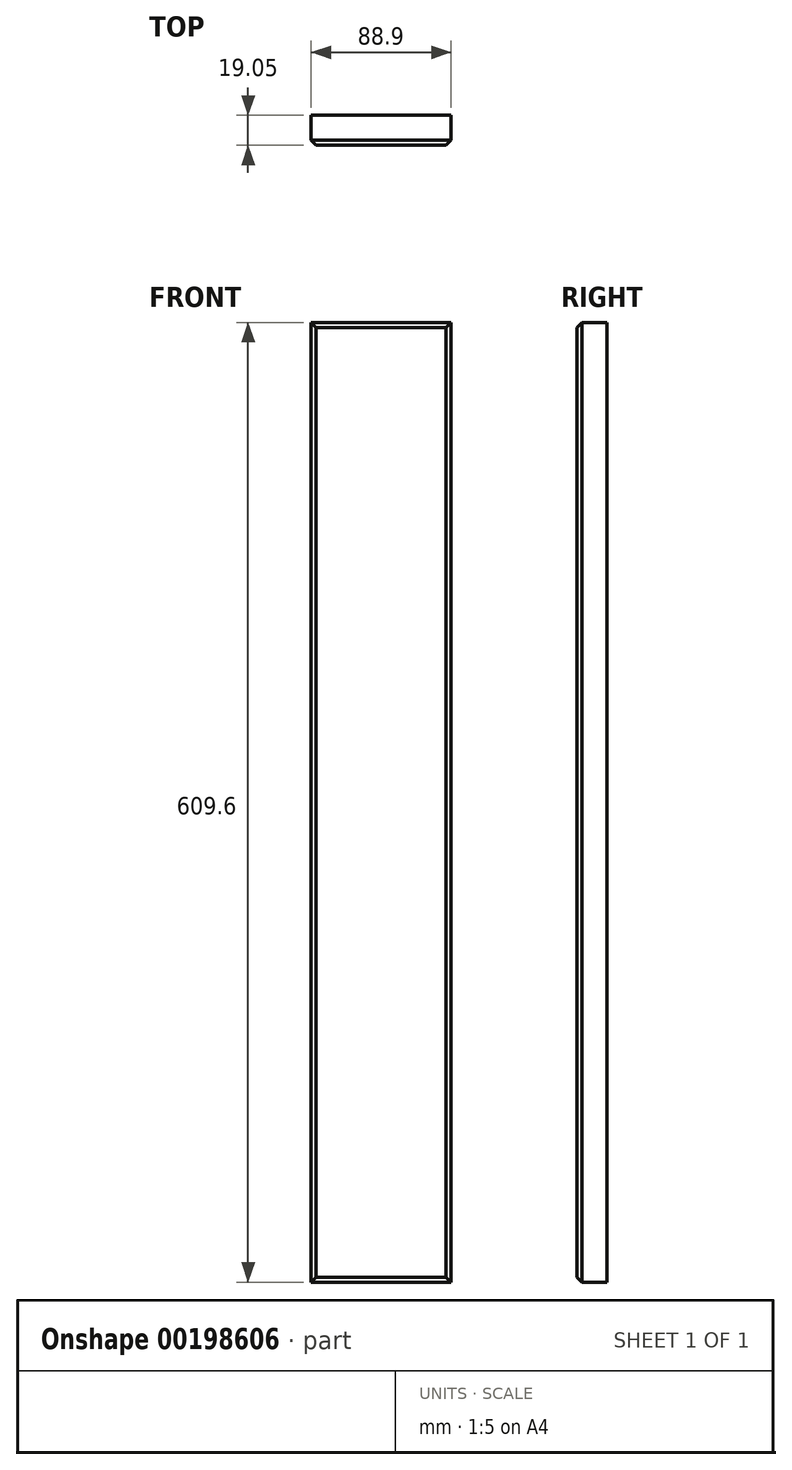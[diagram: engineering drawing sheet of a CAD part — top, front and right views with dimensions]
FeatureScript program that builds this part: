
annotation { "Feature Type Name" : "Feature", "Feature Type Description" : "" }
export const myFeature = defineFeature(function(context is Context, id is Id, definition is map)
    precondition{}
    {
        {
            var Q0;
            Q0=qCreatedBy(makeId("Top.planeOp"),FACE);
            var sketch = newSketch(context, id + "F0", { "sketchPlane" : qUnion([Q0])});
            skLineSegment(sketch, "E0.bottom", {"start": v(0, 0) * mm, "end": v(88.9, 0) * mm});
            skLineSegment(sketch, "E0.top", {"start": v(0, 19.05) * mm, "end": v(88.9, 19.05) * mm});
            skLineSegment(sketch, "E0.left", {"start": v(0, 0) * mm, "end": v(0, 19.05) * mm});
            skLineSegment(sketch, "E0.right", {"start": v(88.9, 0) * mm, "end": v(88.9, 19.05) * mm});
            skSolve(sketch);
        }
        {
            var Q0;
            Q0 = qSketchRegion(id + "F0", true);
            extrude(context, id + "F1", {"entities" : qUnion([Q0]), "depth" : 609.6 * mm});
        }
        {
            var Q0;
            Q0=makeQuery(id+"F1.opExtrude","CAP_EDGE",EDGE,{"disambiguationData":[OSD([sQuery(id+"F0.wireOp",EDGE,"E0.bottom")])],"isStart":false});
            var Q1;
            Q1=makeQuery(id+"F1.opExtrude","SWEPT_EDGE",EDGE,{"disambiguationData":[OSD([sQuery(id+"F0.wireOp",EDGE,"E0.bottom"),sQuery(id+"F0.wireOp",EDGE,"E0.right")])]});
            var Q2;
            Q2=makeQuery(id+"F1.opExtrude","SWEPT_EDGE",EDGE,{"disambiguationData":[OSD([sQuery(id+"F0.wireOp",EDGE,"E0.bottom"),sQuery(id+"F0.wireOp",EDGE,"E0.left")])]});
            var Q3;
            Q3=makeQuery(id+"F1.opExtrude","CAP_EDGE",EDGE,{"disambiguationData":[OSD([sQuery(id+"F0.wireOp",EDGE,"E0.bottom")])],"isStart":true});
            chamfer(context, id + "F2", {"entities" : qUnion([Q0, Q1, Q2, Q3]), "width" : 3.17 * mm, "tangentPropagation" : true});
        }
    });
